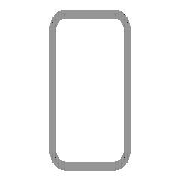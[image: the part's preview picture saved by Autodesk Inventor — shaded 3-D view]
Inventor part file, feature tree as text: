
AUTODESK INVENTOR PART (.ipt)
format: ipt  version: 2022 (Build 260153000, 153)  size: 216,064 bytes
history: native  units: mm (DEFAULTED — no unit token found)
features: other x5, sketch x3, plane x1
ambient origin geometry x8: Origin, YZ Plane, XZ Plane, XY Plane, X Axis, Y Axis, Z Axis, Center Point
bodies: Solid1 (feature_tree), Body (feature_tree), Solid6 (feature_tree)
feature tree (9):
  parser-record x1  (decoder bookkeeping rows leaked as tree rows — omitted from the tree; the rows remain in map.json)
  other  "Driven Length"
  other  "Start Plane"
  other  "End Plane"
  sketch  "Sketch"  dims[d7=7.5mm d10=50.0mm d11=30.0mm d12=5.0mm d13=-22.0mm d14=202.0mm d15=25.0mm d16=15.0mm d17=90.0deg d18=224.0mm]
  sketch  "Sketch3"  dims[d3=224.0mm]
  plane  "Work Plane3"
  sketch  "Sketch4"  dims[d4=0.0mm]
  other  "Srf5"
